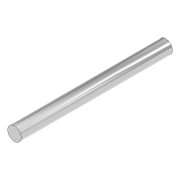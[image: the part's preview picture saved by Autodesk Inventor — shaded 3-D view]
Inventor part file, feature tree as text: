
AUTODESK INVENTOR PART (.ipt)
format: ipt  version: 2020 (Build 240168000, 168)  size: 76,288 bytes
history: native  units: in
note: dims shown in document units (in); Inventor stores cm internally (conversion verified against a paired STEP export)
features: extrude x1, sketch x1
ambient origin geometry x8: Origin, YZ Plane, XZ Plane, XY Plane, X Axis, Y Axis, Z Axis, Center Point
bodies: Solid1 (feature_tree)
feature tree (2):
  extrude  "Extrusion1"  Depth=2.185in TaperAngle=0.0deg
  sketch  "Sketch1"  dims[d0=0.1969in d1=2.185in d2=0.0in]
